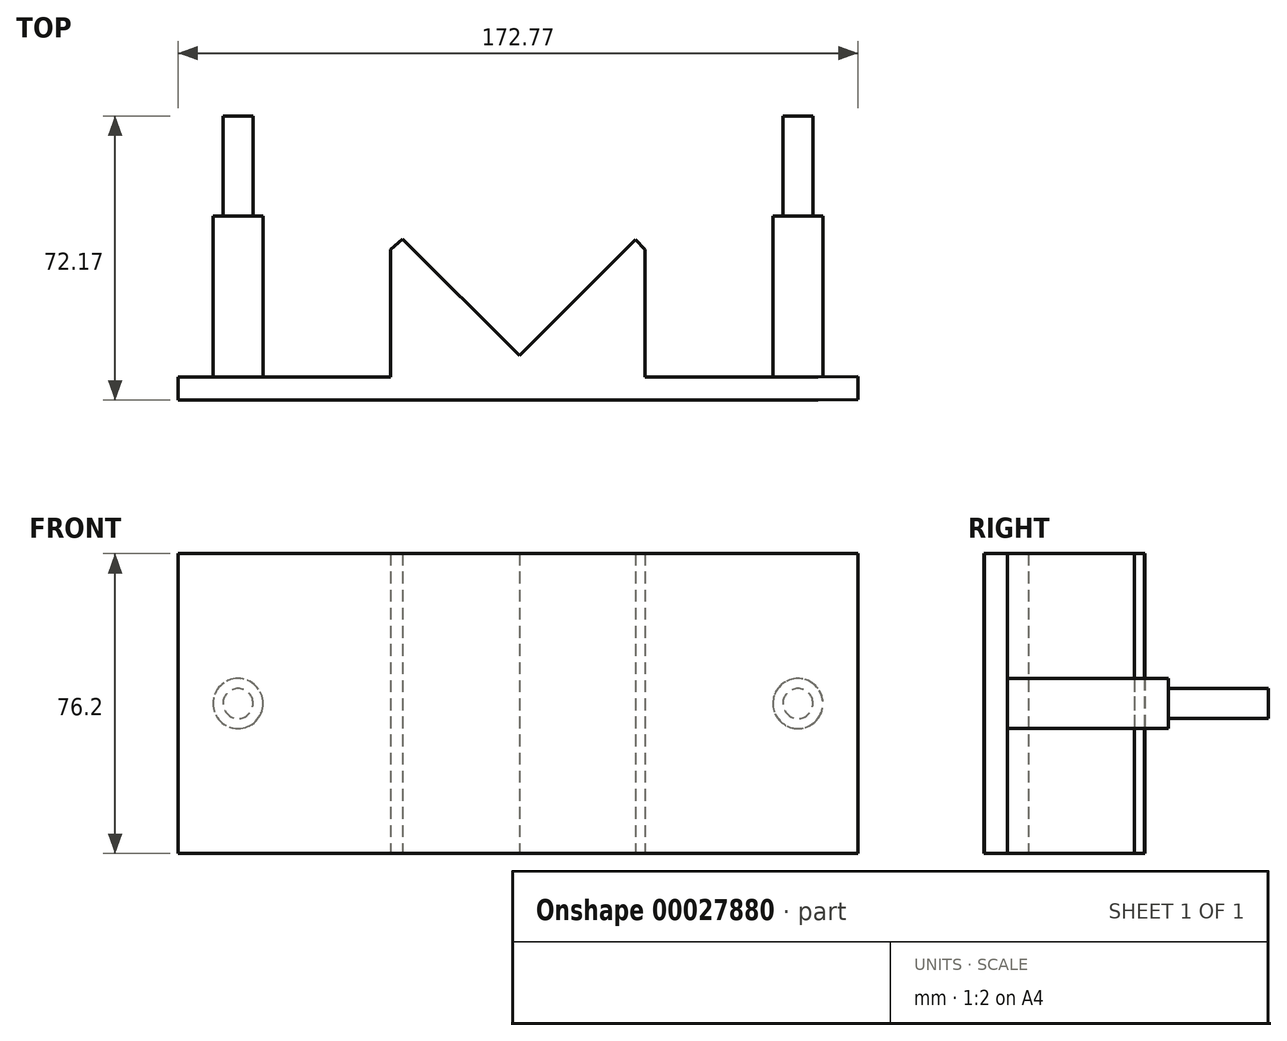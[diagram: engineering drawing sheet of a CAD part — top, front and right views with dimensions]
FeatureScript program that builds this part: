
annotation { "Feature Type Name" : "Feature", "Feature Type Description" : "" }
export const myFeature = defineFeature(function(context is Context, id is Id, definition is map)
    precondition{}
    {
        {
            var Q0;
            Q0=qCreatedBy(makeId("Top.planeOp"),FACE);
            var sketch = newSketch(context, id + "F0", { "sketchPlane" : qUnion([Q0])});
            skLineSegment(sketch, "E0.0", {"start": v(0.36, 5.39) * mm, "end": v(-29.27, 35.02) * mm});
            skLineSegment(sketch, "E0.1", {"start": v(0.36, 5.39) * mm, "end": v(29.82, 34.84) * mm});
            skLineSegment(sketch, "E1", {"start": v(29.82, 34.84) * mm, "end": v(32.33, 32.33) * mm});
            skLineSegment(sketch, "E2", {"start": v(-29.27, 35.02) * mm, "end": v(-32.33, 32.33) * mm});
            skLineSegment(sketch, "E3", {"start": v(-76.2, -5.88) * mm, "end": v(76.25, -5.88) * mm});
            skLineSegment(sketch, "E4.trimOffspring", {"start": v(-32.33, 0) * mm, "end": v(-76.2, 0) * mm});
            skLineSegment(sketch, "E5.trimOffspring", {"start": v(32.33, 0) * mm, "end": v(76.2, 0) * mm});
            skPoint(sketch, "E6.start.orphan", {"position": v(0, 0) * mm});
            skPoint(sketch, "E7", {"position": v(-35.56, 41.3) * mm});
            skLineSegment(sketch, "E8", {"start": v(-35.56, 41.3) * mm, "end": v(-35.56, 0) * mm});
            skLineSegment(sketch, "E9", {"start": v(-76.2, 0) * mm, "end": v(-86.36, 0) * mm});
            skLineSegment(sketch, "E10", {"start": v(-76.2, -5.88) * mm, "end": v(-86.36, -5.88) * mm});
            skLineSegment(sketch, "E11", {"start": v(-86.36, 0) * mm, "end": v(-86.36, -5.88) * mm});
            skLineSegment(sketch, "E12", {"start": v(76.2, 0) * mm, "end": v(86.36, 0.08) * mm});
            skLineSegment(sketch, "E13", {"start": v(76.25, -5.88) * mm, "end": v(86.4, -5.8) * mm});
            skLineSegment(sketch, "E14", {"start": v(86.36, 0.08) * mm, "end": v(86.4, -5.8) * mm});
            skLineSegment(sketch, "E15", {"start": v(-32.33, 32.33) * mm, "end": v(-32.33, 0) * mm});
            skLineSegment(sketch, "E16", {"start": v(32.33, 32.33) * mm, "end": v(32.33, 0) * mm});
            skSolve(sketch);
        }
        {
            var Q0;
            Q0 = qSketchRegion(id + "F0", true);
            extrude(context, id + "F1", {"entities" : qUnion([Q0]), "depth" : 76.2 * mm});
        }
        {
            var Q0;
            Q0=makeQuery(id+"F1.opExtrude","SWEPT_FACE",FACE,{"disambiguationData":[OSD([sQuery(id+"F0.wireOp",EDGE,"E4.trimOffspring")])]});
            var sketch = newSketch(context, id + "F2", { "sketchPlane" : qUnion([Q0])});
            skLineSegment(sketch, "E17", {"start": v(32.33, 38.1) * mm, "end": v(29.79, 38.1) * mm});
            skLineSegment(sketch, "E18", {"start": v(86.36, 38.1) * mm, "end": v(71.12, 38.1) * mm});
            skCircle(sketch, "E19", {"center": v(71.12, 38.1) * mm, "radius": 6.35 * mm});
            skLineSegment(sketch, "E20", {"start": v(0, 0) * mm, "end": v(0, 77.73) * mm, "construction": true});
            skCircle(sketch, "E21.MirrorC", {"center": v(-71.12, 38.1) * mm, "radius": 6.35 * mm});
            skSolve(sketch);
        }
        {
            var Q0;
            Q0 = qSketchRegion(id + "F2", true);
            extrude(context, id + "F3", {"entities" : qUnion([Q0]), "operationType" : NewBodyOperationType.ADD, "depth" : 40.9 * mm});
        }
        {
            var Q0;
            Q0=makeQuery(id+"F3.opExtrude","CAP_FACE",FACE,{"disambiguationData":[OSD([sQuery(id+"F2.wireOp",EDGE,"E19")])],"isStart":false});
            var sketch = newSketch(context, id + "F4", { "sketchPlane" : qUnion([Q0])});
            skCircle(sketch, "E22", {"center": v(71.12, 38.1) * mm, "radius": 3.81 * mm});
            skLineSegment(sketch, "E23", {"start": v(0, 75.9) * mm, "end": v(0, 0) * mm, "construction": true});
            skCircle(sketch, "E24.MirrorC", {"center": v(-71.12, 38.1) * mm, "radius": 3.81 * mm});
            skSolve(sketch);
        }
        {
            var Q0;
            Q0 = qSketchRegion(id + "F4", true);
            extrude(context, id + "F5", {"entities" : qUnion([Q0]), "operationType" : NewBodyOperationType.ADD, "depth" : 25.4 * mm});
        }
    });
